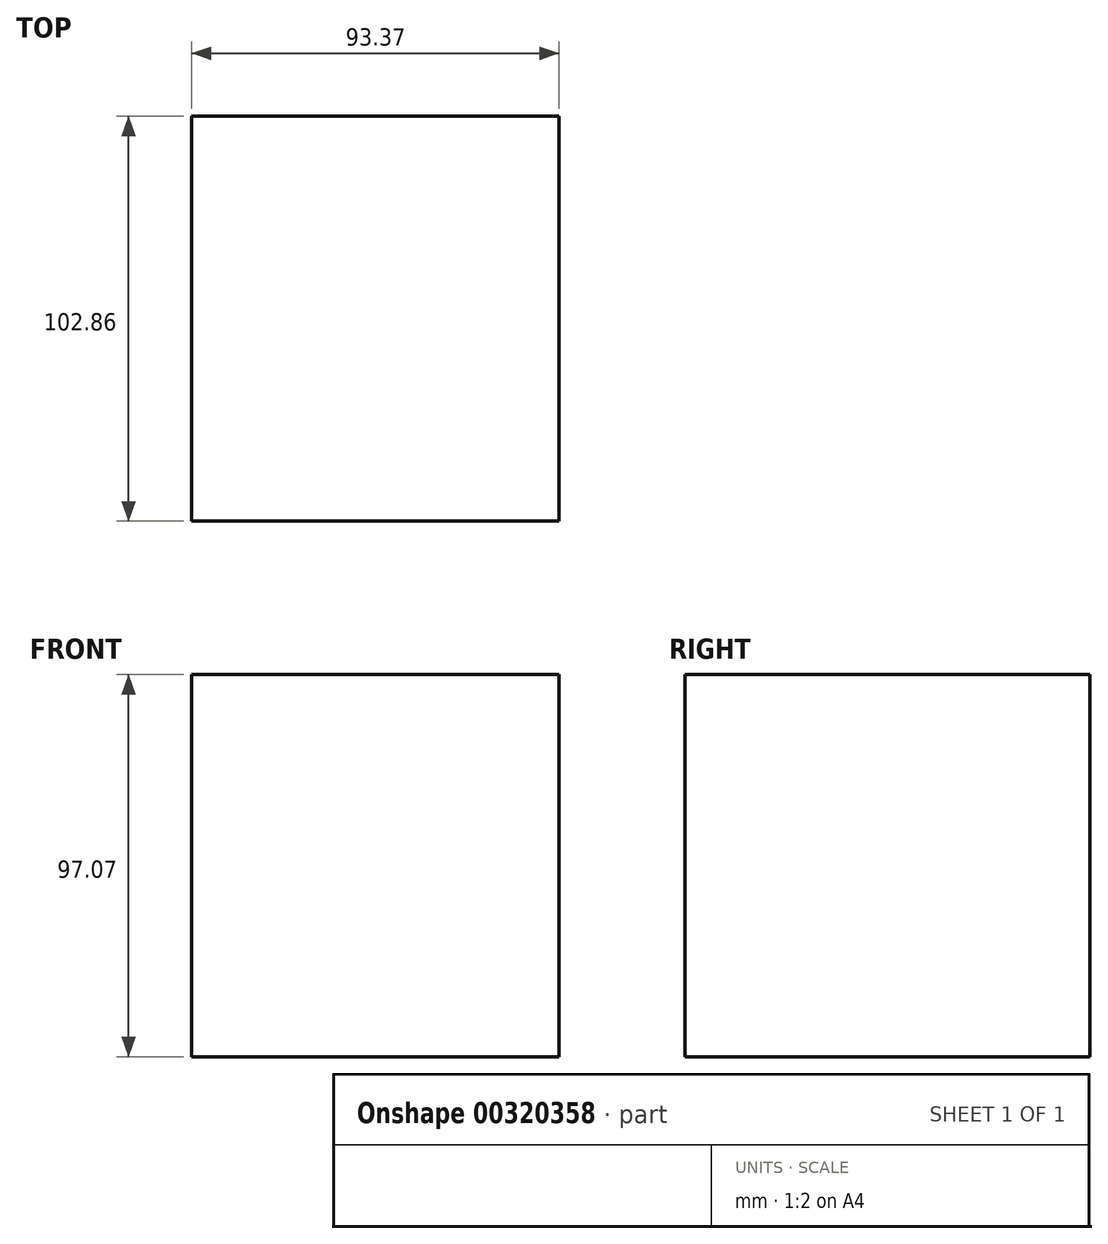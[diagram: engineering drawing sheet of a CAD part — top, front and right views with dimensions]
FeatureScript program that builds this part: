
annotation { "Feature Type Name" : "Feature", "Feature Type Description" : "" }
export const myFeature = defineFeature(function(context is Context, id is Id, definition is map)
    precondition{}
    {
        {
            var Q0;
            Q0=qCreatedBy(makeId("Front.planeOp"),FACE);
            var sketch = newSketch(context, id + "F0", { "sketchPlane" : qUnion([Q0])});
            skLineSegment(sketch, "E0.bottom", {"start": v(-46.62, -30.63) * mm, "end": v(46.75, -30.63) * mm});
            skLineSegment(sketch, "E0.top", {"start": v(-46.62, 66.44) * mm, "end": v(46.75, 66.44) * mm});
            skLineSegment(sketch, "E0.left", {"start": v(-46.62, -30.63) * mm, "end": v(-46.62, 66.44) * mm});
            skLineSegment(sketch, "E0.right", {"start": v(46.75, -30.63) * mm, "end": v(46.75, 66.44) * mm});
            skSolve(sketch);
        }
        {
            var Q0;
            Q0=makeQuery(id+"F0.imprint","IMPRINT",FACE,{"disambiguationData":[TD([[makeQuery(id+"F0.imprint","IMPRINT",EDGE,{"derivedFrom":sQuery(id+"F0.wireOp",EDGE,"E0.bottom")}),1.0]])]});
            extrude(context, id + "F1", {"entities" : qUnion([Q0]), "depth" : 50.16 * mm});
        }
        {
            var Q0;
            Q0=makeQuery(id+"F1.opExtrude","CAP_FACE",FACE,{"disambiguationData":[OSD([sQuery(id+"F0.wireOp",EDGE,"E0.bottom"),sQuery(id+"F0.wireOp",EDGE,"E0.top"),sQuery(id+"F0.wireOp",EDGE,"E0.left"),sQuery(id+"F0.wireOp",EDGE,"E0.right")])],"isStart":true});
            extrude(context, id + "F2", {"entities" : qUnion([Q0]), "operationType" : NewBodyOperationType.ADD, "depth" : 52.7 * mm});
        }
    });
